# Revit family: NBS_WallgateLtd_PrxmtySnsrCtrlUnits_WDC1002
name_source: partatom
category: Mechanical Equipment
revit_build: Autodesk Revit 2014 (Build: 20130709_2115(x64)
units: mm (PartAtom-declared; Revit-internal decimal feet)

## types (1)
- WDC100
    AccessoryOptions = CISTFV Electronic cisterns, FVA Non-Potable Direct Flush Valves, DFKIT Potable Direct Flush Valves, WVC Flush Valve Cables, PBA Piezo Touch Buttons, PBA-IR Infra-Red Activation Sensors, WVPB Basin Water Valve Pack, WVPS Shower Water Valve Pack, CLS Key Lock Switches
    ApplicationOptions = Central or stand alone
    AssetType = Fixed
    BIMObjectName = NBS_WallgateLtd_ProximitySensorControlUnits_WDC100
    ControlType = Unset
    Description = Fully programmable four channel electronic controller to manage all sanitary ware within one room, typically; 1 x Basins, 1 x WC's & 1 x Showers
    DurationUnit = year
    ElectricalDeviceNominalPower = 50
    Features = Highly energy and water efficient, easily programmable - locally or networked
    HasProtectiveEarth = Yes
    IP_Code = IP55
    IfcExportAs = IfcControllerType
    IfcExportType = NOTDEFINED
    InsulationStandardClass = Class 1
    ManufacturerName = Wallgate Ltd
    ManufacturerURL = www.wallgate.com
    ModelNumber = WDC100
    Mounting = Wall mounted
    NBSCertification = www.nationalbimlibrary.com/cert/pif20o1s
    NBSDescription = Proximity sensor control units
    NBSReference = 45-35-70/422
    Name = ProximitySensorControlUnits_WDC100_WallgateLtd
    NominalCurrent = 1
    NominalFrequencyRange = 50.0 , 60.0
    NominalHeight = 150 mm
    NominalLength = 90 mm
    NominalVoltage = 110.0 , 240.0
    NominalWidth = 200 mm
    NumberOfPoles = 0
    OutletNumber = 4
    PhaseAngle = 0.00°
    PhaseReference = Single phase
    ProductInformation = www.wallgate.com/products/washroom-controls/wdc-electronic-controller-range
    SensorControlMaterial = NBS_Concept
    SignalFactor = 0
    SignalOffset = 0
    SignalTime = 0
    Size = 200 x 150 x 90 mm
    ThirdPartyCertification = CE marked, SAA Approved
    Uniclass2 = 45-51-53/465
    UsageCurrent = 1
    Version = 1
    WarrantyDurationParts = 1
    WarrantyDurationUnit = year
    Weight = 1.7 kg

## geometry (parser evidence)
native form markers: Sweep x2
no freeform markers — native parametric forms only
